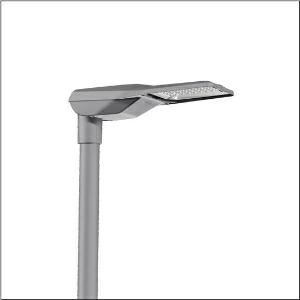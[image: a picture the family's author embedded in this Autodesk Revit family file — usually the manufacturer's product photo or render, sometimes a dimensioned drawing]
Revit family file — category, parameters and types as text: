
# Revit family: streetlight_sl_21_iq_mini___st0_5a_5xe2b31d08jb_7d26
name_source: partatom
category: Lighting Fixtures
units: mm (PartAtom-declared; Revit-internal decimal feet)

## family parameters
Cut with Voids When Loaded = No
Host = Face
Light Source = No
Part Type = Normal
Room Calculation Point = No
Round Connector Dimension = Use Diameter
Shared = No

## types (1)
- --- (1 x LED, 10820 lm, 71.6 W, 3000K)
    Apparent Load = 72 VA
    CIE Flux Codes = 43 76 97 100 100
    Color Rendering = 70
    Color Temperature = 3000K
    Default Elevation = 1800 mm
    Description = Streetlight SL 21 iQ mini, mast luminaire, primary light control with lens, of PMMA, primary optical cover: cover, of toughened safety glass, transparent, light distribution: ST0.5a, light emission: direct distribution, primary light characteristic: asymmetric, installation type: post-top, side-entry, LED, High Power LED, rated luminous flux: 10.820lm, luminous efficacy: 151lm/W, light colour: 730, colour temperature: 3000K, control: Auto-Match, Temp-Guard, Lumen-Switch, Night-Set, Smart-Wire, Light-Fading, Desk-Remote (wireless, voltage-free reading and setting of iQ features in the workshop via application-optimized NFC function/RFID function), optimised constant luminous flux control (CLO 2.0), presetting dimming linear, mains connection: 220..240V, AC, 50/60Hz, start of lifetime: 72W, end of service life: 75W, reduction: 33W, luminaire housing, of diecast aluminium, powder-coated, Siteco® metallic grey (DB 702S), corrosivity category C5 mid according to DIN EN ISO 12944, please order mast flange separately, inclination adjustable: 0°, 5°, 10°, 15°, sealing non-destructively replaceable, multi-level sealing system, length: 628mm, width: 235mm, height: 110mm, mast flange for spigot size: 42mm (side-entry): 5XC10008XM4, 60/48mm (side-entry/post-top): 5XC10108XM2, 76/60mm (side-entry/post-top): 5XC10108XM1, protection rating (complete): IP66, insulation class (complete): insulation class II (safety insulation), certification: CE, ENEC, ENEC+, VDE, impact resistance: IK09, permissible operating ambient temperature for outdoor applications: -40..+50°C, standard-compliant lighting for roads and squares, packaging unit: 1 piece

Light Distribution: ST0.5a
    Height = 110 mm
    Lamp = 1 x LED
    Lamp Light Flux = 10820 lm
    Lamp Power = 71.6 W
    Lamp count = 1
    Length = 625 mm
    Luminous efficacy = 151 lm/W
    Manufacturer = Siteco
    ModVariant = No
    Model = 5XE2B31D08JB
    Number of Poles = 1
    OnlyDefault = Yes
    Power Factor = 1
    Product Name = Streetlight SL 21 iQ mini | ST0.5a
    Product group = mast luminaire | pylon top
    ProductGroupID = 6100
    Protection Class = Protection class II
    Protection Degree = IP 66
    RLX_Detail_Level = 1
    RLX_Emergency_Light_Flux = 0 lm
    RLX_Emergency_Type = 0
    RLX_Emergency_Type_DB = No
    RlxData = <blob elided: 103441 chars, md5=e55f0f37>
    Socket = socket
    Standby Power = 0 W
    System Light Flux = 10820 lm
    System Power = 72 W
    Type Comments = factory setting: luminous flux: 100 % | dim-lin: 254 | 746 mA
    Type Image = l_1003519.jpg
    URL = http://relux.com
    VarID = @adj_104891
    Voltage = 0 V
    Weight = 0.00 kg
    Width = 234 mm

## geometry (parser evidence)
native form markers: Blend x4, Sweep x9
no freeform markers — native parametric forms only
